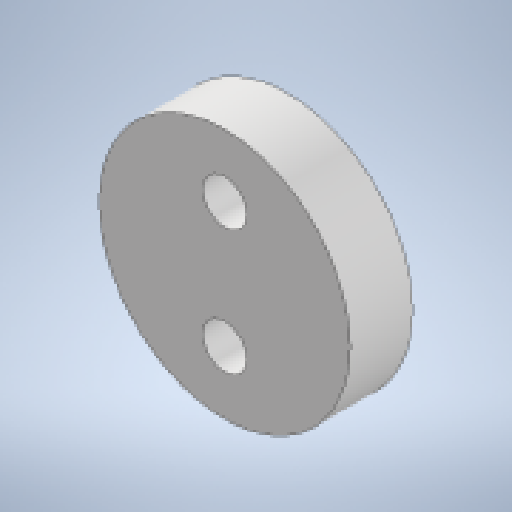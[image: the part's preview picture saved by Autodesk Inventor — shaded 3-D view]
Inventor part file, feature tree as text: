
AUTODESK INVENTOR PART (.ipt)
format: ipt  version: 2023 (Build 270158000, 158)  size: 167,936 bytes
history: native  units: in
note: dims shown in document units (in); Inventor stores cm internally (conversion verified against a paired STEP export)
features: extrude x4, sketch x4, chamfer x1
ambient origin geometry x8: Origin, YZ Plane, XZ Plane, XY Plane, X Axis, Y Axis, Z Axis, Center Point
bodies: Solid1 (feature_tree)
feature tree (9):
  extrude  "Extrusion1"  Depth=0.4331in TaperAngle=0.0deg
  extrude  "Extrusion4"  Depth=0.1378in
  extrude  "Extrusion2"  Depth=0.1575in
  extrude  "Extrusion3"  Depth=0.1969in
  chamfer  "Chamfer1"  Distance=0.1654in
  sketch  "Sketch2"  dims[d0=0.748in d1=0.4331in d2=0.0in]
  sketch  "Sketch3"  dims[d3=0.1378in d4=0.1378in]
  sketch  "Sketch4"  dims[d5=0.315in d6=0.1575in]
  sketch  "Sketch5"  dims[d7=0.0in d8=0.0in d9=0.1654in d10=0.1654in d11=0.7874in d12=0.1969in d13=0.0in d14=0.0197in d15=0.0787in d16=45.0deg d17=1.1811in d18=0.1969in d19=0.0in]
